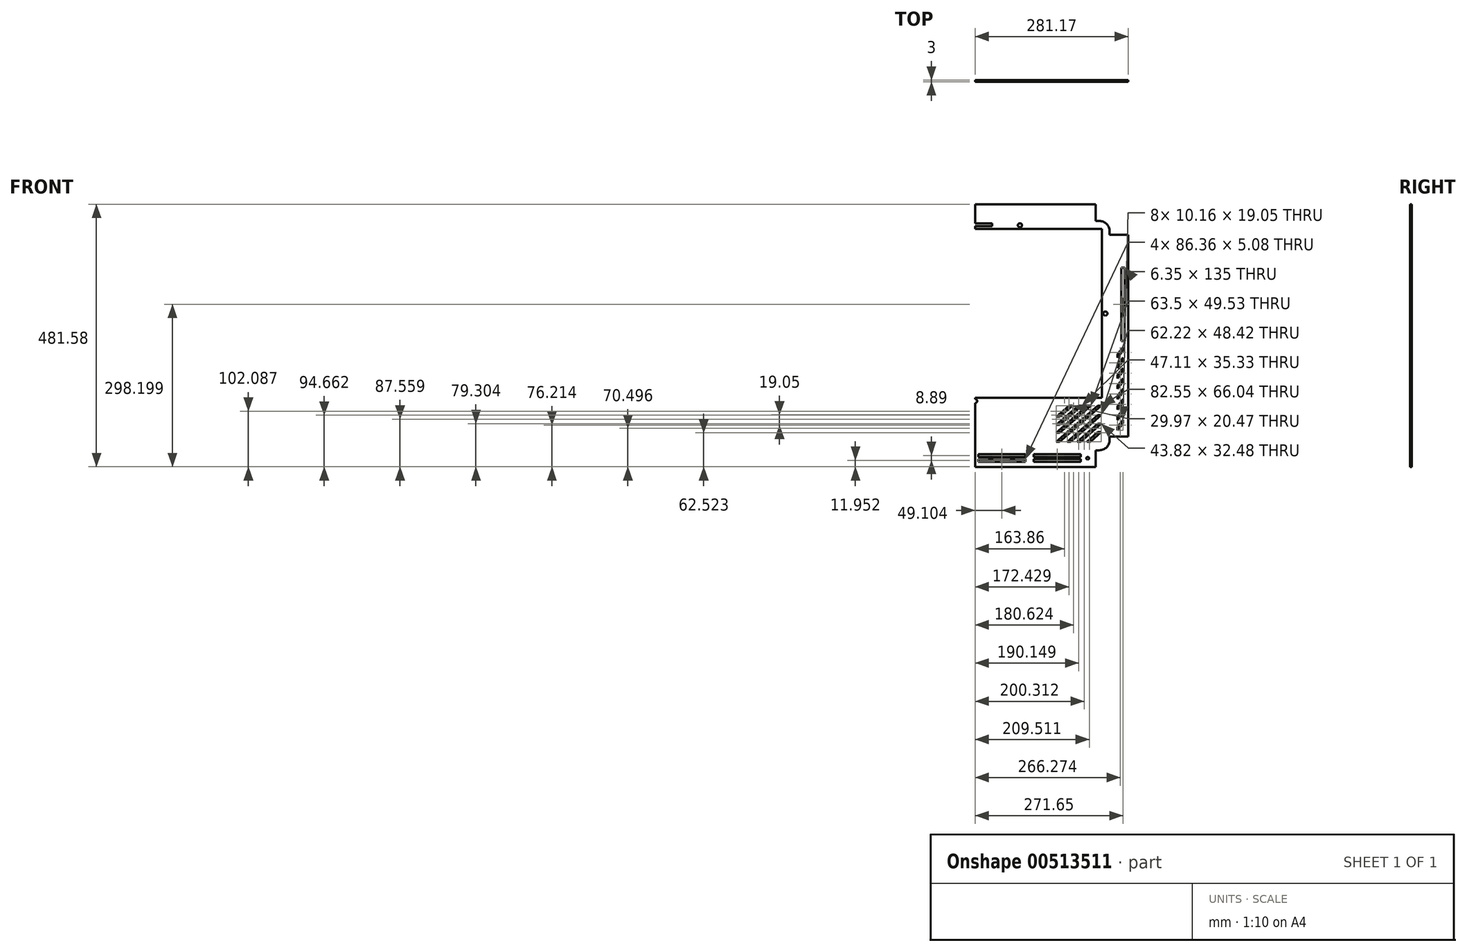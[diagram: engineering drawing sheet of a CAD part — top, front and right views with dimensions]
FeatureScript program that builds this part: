
annotation { "Feature Type Name" : "Feature", "Feature Type Description" : "" }
export const myFeature = defineFeature(function(context is Context, id is Id, definition is map)
    precondition{}
    {
        {
            var Q0;
            Q0=qCreatedBy(makeId("Front.planeOp"),FACE);
            var sketch = newSketch(context, id + "F0", { "sketchPlane" : qUnion([Q0])});
            skLineSegment(sketch, "E0", {"start": v(0.65, 216.03) * mm, "end": v(0.65, 185.55) * mm});
            skLineSegment(sketch, "E1", {"start": v(0.65, -265.55) * mm, "end": v(0.65, -235.07) * mm});
            skLineSegment(sketch, "E2.left", {"start": v(0.65, -235.07) * mm, "end": v(0.65, 185.55) * mm});
            skArc(sketch, "E3.MirrorCS", {"start": v(228.48, 185.55) * mm, "mid": v(241.95, 179.97) * mm, "end": v(247.53, 166.5) * mm});
            skPoint(sketch, "E4.MirrorP", {"position": v(243.47, 178.95) * mm});
            skArc(sketch, "E5.MirrorCS", {"start": v(247.53, -216.02) * mm, "mid": v(241.95, -229.5) * mm, "end": v(228.48, -235.07) * mm});
            skLineSegment(sketch, "E6.MirrorCS", {"start": v(0.65, 185.55) * mm, "end": v(228.48, 185.55) * mm});
            skLineSegment(sketch, "E7.MirrorCS", {"start": v(247.53, -216.02) * mm, "end": v(247.53, 166.5) * mm});
            skPoint(sketch, "E8.MirrorP", {"position": v(247.53, 185.55) * mm});
            skLineSegment(sketch, "E9.MirrorCS", {"start": v(222.13, -235.07) * mm, "end": v(0.65, -235.07) * mm});
            skPoint(sketch, "E10.MirrorP", {"position": v(247.53, -237.61) * mm});
            skLineSegment(sketch, "E11.MirrorCS", {"start": v(281.82, 160.15) * mm, "end": v(247.53, 160.15) * mm});
            skLineSegment(sketch, "E12.MirrorCS", {"start": v(281.82, -209.67) * mm, "end": v(247.53, -209.67) * mm});
            skLineSegment(sketch, "E13.MirrorCS", {"start": v(281.82, 160.15) * mm, "end": v(281.82, -209.67) * mm});
            skLineSegment(sketch, "E14.MirrorCS", {"start": v(247.53, 160.15) * mm, "end": v(247.53, -209.67) * mm});
            skLineSegment(sketch, "E15.MirrorCS", {"start": v(222.13, 216.03) * mm, "end": v(0.65, 216.03) * mm});
            skLineSegment(sketch, "E16.MirrorCS", {"start": v(222.13, 216.03) * mm, "end": v(222.13, 185.55) * mm});
            skLineSegment(sketch, "E17.MirrorCS", {"start": v(222.13, -265.55) * mm, "end": v(0.65, -265.55) * mm});
            skLineSegment(sketch, "E18.MirrorCS", {"start": v(222.13, -235.07) * mm, "end": v(222.13, -265.55) * mm});
            skLineSegment(sketch, "E19.MirrorCS", {"start": v(203.08, 185.55) * mm, "end": v(0.65, 185.55) * mm});
            skLineSegment(sketch, "E20.MirrorCS", {"start": v(0.65, -235.07) * mm, "end": v(228.48, -235.07) * mm});
            skPoint(sketch, "E21.MirrorP", {"position": v(247.53, -235.07) * mm});
            skSolve(sketch);
        }
        {
            var Q0;
            Q0 = qSketchRegion(id + "F0", true);
            extrude(context, id + "F1", {"entities" : qUnion([Q0]), "depth" : 3 * mm, "offsetDistance" : 25.4 * mm});
        }
        {
            var Q0;
            Q0=qCreatedBy(makeId("Front.planeOp"),FACE);
            var sketch = newSketch(context, id + "F2", { "sketchPlane" : qUnion([Q0])});
            skLineSegment(sketch, "E22.MirrorCS", {"start": v(261.84, -116.31) * mm, "end": v(261.84, -122.66) * mm});
            skLineSegment(sketch, "E23.MirrorCS", {"start": v(261.84, -135.36) * mm, "end": v(261.84, -141.71) * mm});
            skLineSegment(sketch, "E24.MirrorCS", {"start": v(272, -90.91) * mm, "end": v(272, -84.56) * mm});
            skLineSegment(sketch, "E25.MirrorCS", {"start": v(261.84, -84.56) * mm, "end": v(272, -71.86) * mm});
            skLineSegment(sketch, "E26.MirrorCS", {"start": v(261.84, -160.76) * mm, "end": v(261.84, -154.41) * mm});
            skLineSegment(sketch, "E27.MirrorCS", {"start": v(272, -84.56) * mm, "end": v(261.84, -97.26) * mm});
            skLineSegment(sketch, "E28.MirrorCS", {"start": v(272, -71.86) * mm, "end": v(272, -65.51) * mm});
            skLineSegment(sketch, "E29.MirrorCS", {"start": v(261.84, -78.21) * mm, "end": v(261.84, -84.56) * mm});
            skLineSegment(sketch, "E30.MirrorCS", {"start": v(261.84, -59.16) * mm, "end": v(261.84, -65.51) * mm});
            skLineSegment(sketch, "E31.MirrorCS", {"start": v(261.84, -141.71) * mm, "end": v(272, -129.01) * mm});
            skLineSegment(sketch, "E32.MirrorCS", {"start": v(261.84, -103.61) * mm, "end": v(272, -90.91) * mm});
            skLineSegment(sketch, "E33.MirrorCS", {"start": v(261.84, -122.66) * mm, "end": v(272, -109.96) * mm});
            skLineSegment(sketch, "E34.MirrorCS", {"start": v(272, -129.01) * mm, "end": v(272, -122.66) * mm});
            skLineSegment(sketch, "E35.MirrorCS", {"start": v(261.84, -154.41) * mm, "end": v(272, -141.71) * mm});
            skLineSegment(sketch, "E36.MirrorCS", {"start": v(272, -160.76) * mm, "end": v(261.84, -173.46) * mm});
            skLineSegment(sketch, "E37.MirrorCS", {"start": v(261.84, -173.46) * mm, "end": v(261.84, -179.81) * mm});
            skLineSegment(sketch, "E38.MirrorCS", {"start": v(261.84, -179.81) * mm, "end": v(272, -167.11) * mm});
            skLineSegment(sketch, "E39.MirrorCS", {"start": v(272, -179.81) * mm, "end": v(272, -186.16) * mm});
            skLineSegment(sketch, "E40.MirrorCS", {"start": v(272, -109.96) * mm, "end": v(272, -103.61) * mm});
            skLineSegment(sketch, "E41.MirrorCS", {"start": v(272, -167.11) * mm, "end": v(272, -160.76) * mm});
            skLineSegment(sketch, "E42.MirrorCS", {"start": v(261.84, -97.26) * mm, "end": v(261.84, -103.61) * mm});
            skLineSegment(sketch, "E43.MirrorCS", {"start": v(272, -122.66) * mm, "end": v(261.84, -135.36) * mm});
            skLineSegment(sketch, "E44.MirrorCS", {"start": v(272, -65.51) * mm, "end": v(261.84, -78.21) * mm});
            skLineSegment(sketch, "E45.MirrorCS", {"start": v(272, -141.71) * mm, "end": v(272, -148.06) * mm});
            skLineSegment(sketch, "E46.MirrorCS", {"start": v(272, -103.61) * mm, "end": v(261.84, -116.31) * mm});
            skLineSegment(sketch, "E47.MirrorCS", {"start": v(272, -148.06) * mm, "end": v(261.84, -160.76) * mm});
            skLineSegment(sketch, "E48.MirrorCS", {"start": v(92.93, -242.17) * mm, "end": v(92.93, -247.25) * mm});
            skLineSegment(sketch, "E49.MirrorCS", {"start": v(261.84, -65.51) * mm, "end": v(272, -52.81) * mm});
            skLineSegment(sketch, "E50.MirrorCS", {"start": v(92.93, -251.06) * mm, "end": v(92.93, -256.14) * mm});
            skLineSegment(sketch, "E51.MirrorCS", {"start": v(272, -186.16) * mm, "end": v(261.84, -198.86) * mm});
            skLineSegment(sketch, "E52.MirrorCS", {"start": v(261.84, -198.86) * mm, "end": v(261.84, -192.51) * mm});
            skLineSegment(sketch, "E53.MirrorCS", {"start": v(261.84, -192.51) * mm, "end": v(272, -179.81) * mm});
            skLineSegment(sketch, "E54.MirrorCS", {"start": v(194.53, -251.06) * mm, "end": v(194.53, -256.14) * mm});
            skLineSegment(sketch, "E55.MirrorCS", {"start": v(194.53, -247.25) * mm, "end": v(194.53, -242.17) * mm});
            skLineSegment(sketch, "E56.MirrorCS", {"start": v(272, -52.81) * mm, "end": v(272, -46.46) * mm});
            skLineSegment(sketch, "E57.MirrorCS", {"start": v(108.17, -242.17) * mm, "end": v(108.17, -247.25) * mm});
            skLineSegment(sketch, "E58.MirrorCS", {"start": v(108.17, -256.14) * mm, "end": v(108.17, -251.06) * mm});
            skLineSegment(sketch, "E59.MirrorCS", {"start": v(272, -46.46) * mm, "end": v(261.84, -59.16) * mm});
            skLineSegment(sketch, "E60.MirrorCS", {"start": v(6.57, -256.14) * mm, "end": v(6.57, -251.06) * mm});
            skLineSegment(sketch, "E61.MirrorCS", {"start": v(6.57, -247.25) * mm, "end": v(6.57, -242.17) * mm});
            skLineSegment(sketch, "E62.MirrorCS", {"start": v(6.57, -251.06) * mm, "end": v(92.93, -251.06) * mm});
            skCircle(sketch, "E63.MirrorC", {"center": v(207.23, -249.79) * mm, "radius": 2.5 * mm});
            skLineSegment(sketch, "E64.MirrorCS", {"start": v(194.53, -242.17) * mm, "end": v(108.17, -242.17) * mm});
            skLineSegment(sketch, "E65.MirrorCS", {"start": v(194.53, -256.14) * mm, "end": v(108.17, -256.14) * mm});
            skLineSegment(sketch, "E66.MirrorCS", {"start": v(92.93, -256.14) * mm, "end": v(6.57, -256.14) * mm});
            skLineSegment(sketch, "E67.MirrorCS", {"start": v(92.93, -247.25) * mm, "end": v(6.57, -247.25) * mm});
            skLineSegment(sketch, "E68.MirrorCS", {"start": v(108.17, -247.25) * mm, "end": v(194.53, -247.25) * mm});
            skLineSegment(sketch, "E69.MirrorCS", {"start": v(108.17, -251.06) * mm, "end": v(194.53, -251.06) * mm});
            skLineSegment(sketch, "E70.MirrorCS", {"start": v(6.57, -242.17) * mm, "end": v(92.93, -242.17) * mm});
            skLineSegment(sketch, "E71.bottom", {"start": v(233.31, 171.33) * mm, "end": v(-40.62, 171.33) * mm});
            skLineSegment(sketch, "E71.top", {"start": v(233.31, -138.55) * mm, "end": v(-40.62, -138.55) * mm});
            skLineSegment(sketch, "E71.left", {"start": v(233.31, 171.33) * mm, "end": v(233.31, -138.55) * mm});
            skLineSegment(sketch, "E71.right", {"start": v(-40.62, 171.33) * mm, "end": v(-40.62, -138.55) * mm});
            skLineSegment(sketch, "E72.bottom", {"start": v(275.47, 100.15) * mm, "end": v(269.12, 100.15) * mm});
            skLineSegment(sketch, "E72.top", {"start": v(275.47, -34.85) * mm, "end": v(269.12, -34.85) * mm});
            skLineSegment(sketch, "E72.left", {"start": v(275.47, 100.15) * mm, "end": v(275.47, -34.85) * mm});
            skLineSegment(sketch, "E72.right", {"start": v(269.12, 100.15) * mm, "end": v(269.12, -34.85) * mm});
            skCircle(sketch, "E73", {"center": v(82.94, 177.68) * mm, "radius": 3.81 * mm});
            skLineSegment(sketch, "E74.bottom", {"start": v(-8.76, 181.49) * mm, "end": v(32.14, 181.49) * mm});
            skLineSegment(sketch, "E74.top", {"start": v(-8.76, 176.4) * mm, "end": v(32.14, 176.4) * mm});
            skLineSegment(sketch, "E74.left", {"start": v(-8.76, 181.49) * mm, "end": v(-8.76, 176.4) * mm});
            skLineSegment(sketch, "E74.right", {"start": v(32.14, 181.49) * mm, "end": v(32.14, 176.4) * mm});
            skCircle(sketch, "E75", {"center": v(239.66, 15.73) * mm, "radius": 3.81 * mm});
            skCircle(sketch, "E76", {"center": v(0.65, -144.9) * mm, "radius": 3.81 * mm});
            skSolve(sketch);
        }
        {
            var Q0;
            Q0 = qSketchRegion(id + "F2", true);
            extrude(context, id + "F3", {"entities" : qUnion([Q0]), "operationType" : NewBodyOperationType.REMOVE, "depth" : 25.4 * mm, "offsetDistance" : 25.4 * mm});
        }
        {
            var Q0;
            Q0=qCreatedBy(makeId("Front.planeOp"),FACE);
            var sketch = newSketch(context, id + "F4", { "sketchPlane" : qUnion([Q0])});
            skLineSegment(sketch, "E77.MirrorCS", {"start": v(213.02, -153.23) * mm, "end": v(206.67, -153.23) * mm});
            skLineSegment(sketch, "E78.MirrorCS", {"start": v(232.07, -153.23) * mm, "end": v(225.72, -153.23) * mm});
            skLineSegment(sketch, "E79.MirrorCS", {"start": v(196.63, -153.23) * mm, "end": v(190.28, -153.23) * mm});
            skLineSegment(sketch, "E80.MirrorCS", {"start": v(149.52, -173.7) * mm, "end": v(155.87, -173.7) * mm});
            skLineSegment(sketch, "E81.MirrorCS", {"start": v(179.5, -153.23) * mm, "end": v(173.15, -153.23) * mm});
            skLineSegment(sketch, "E82.MirrorCS", {"start": v(232.07, -186.79) * mm, "end": v(225.72, -186.79) * mm});
            skLineSegment(sketch, "E83.MirrorCS", {"start": v(169.85, -219.27) * mm, "end": v(176.2, -219.27) * mm});
            skLineSegment(sketch, "E84.MirrorCS", {"start": v(149.52, -202.76) * mm, "end": v(155.87, -202.76) * mm});
            skLineSegment(sketch, "E85.MirrorCS", {"start": v(149.52, -219.27) * mm, "end": v(155.87, -219.27) * mm});
            skLineSegment(sketch, "E86.MirrorCS", {"start": v(205.76, -219.27) * mm, "end": v(212.1, -219.27) * mm});
            skLineSegment(sketch, "E87.MirrorCS", {"start": v(149.52, -188.55) * mm, "end": v(155.87, -188.55) * mm});
            skLineSegment(sketch, "E88.MirrorCS", {"start": v(232.07, -201.96) * mm, "end": v(225.72, -201.96) * mm});
            skLineSegment(sketch, "E89.MirrorCS", {"start": v(232.07, -170.84) * mm, "end": v(225.72, -170.84) * mm});
            skLineSegment(sketch, "E90.MirrorCS", {"start": v(188.25, -219.27) * mm, "end": v(194.6, -219.27) * mm});
            skLineSegment(sketch, "E91.MirrorCS", {"start": v(225.72, -201.96) * mm, "end": v(205.76, -219.27) * mm});
            skLineSegment(sketch, "E92.MirrorCS", {"start": v(155.87, -219.27) * mm, "end": v(232.07, -153.23) * mm});
            skLineSegment(sketch, "E93.MirrorCS", {"start": v(190.28, -153.23) * mm, "end": v(149.52, -188.55) * mm});
            skLineSegment(sketch, "E94.MirrorCS", {"start": v(225.72, -153.23) * mm, "end": v(149.52, -219.27) * mm});
            skLineSegment(sketch, "E95.MirrorCS", {"start": v(194.6, -219.27) * mm, "end": v(232.07, -186.79) * mm});
            skLineSegment(sketch, "E96.MirrorCS", {"start": v(225.72, -186.79) * mm, "end": v(188.25, -219.27) * mm});
            skLineSegment(sketch, "E97.MirrorCS", {"start": v(155.87, -173.7) * mm, "end": v(179.5, -153.23) * mm});
            skLineSegment(sketch, "E98.MirrorCS", {"start": v(212.1, -219.27) * mm, "end": v(232.07, -201.96) * mm});
            skLineSegment(sketch, "E99.MirrorCS", {"start": v(155.87, -202.76) * mm, "end": v(213.02, -153.23) * mm});
            skLineSegment(sketch, "E100.MirrorCS", {"start": v(173.15, -153.23) * mm, "end": v(149.52, -173.7) * mm});
            skPoint(sketch, "E101.MirrorP", {"position": v(152.7, -219.27) * mm});
            skLineSegment(sketch, "E102.MirrorCS", {"start": v(176.2, -219.27) * mm, "end": v(232.07, -170.84) * mm});
            skLineSegment(sketch, "E103.MirrorCS", {"start": v(155.87, -188.55) * mm, "end": v(196.63, -153.23) * mm});
            skLineSegment(sketch, "E104.MirrorCS", {"start": v(225.72, -170.84) * mm, "end": v(169.85, -219.27) * mm});
            skLineSegment(sketch, "E105.MirrorCS", {"start": v(206.67, -153.23) * mm, "end": v(149.52, -202.76) * mm});
            skSolve(sketch);
        }
        {
            var Q0;
            Q0 = qSketchRegion(id + "F4", true);
            extrude(context, id + "F5", {"entities" : qUnion([Q0]), "operationType" : NewBodyOperationType.REMOVE, "depth" : 25.4 * mm, "offsetDistance" : 25.4 * mm});
        }
    });
